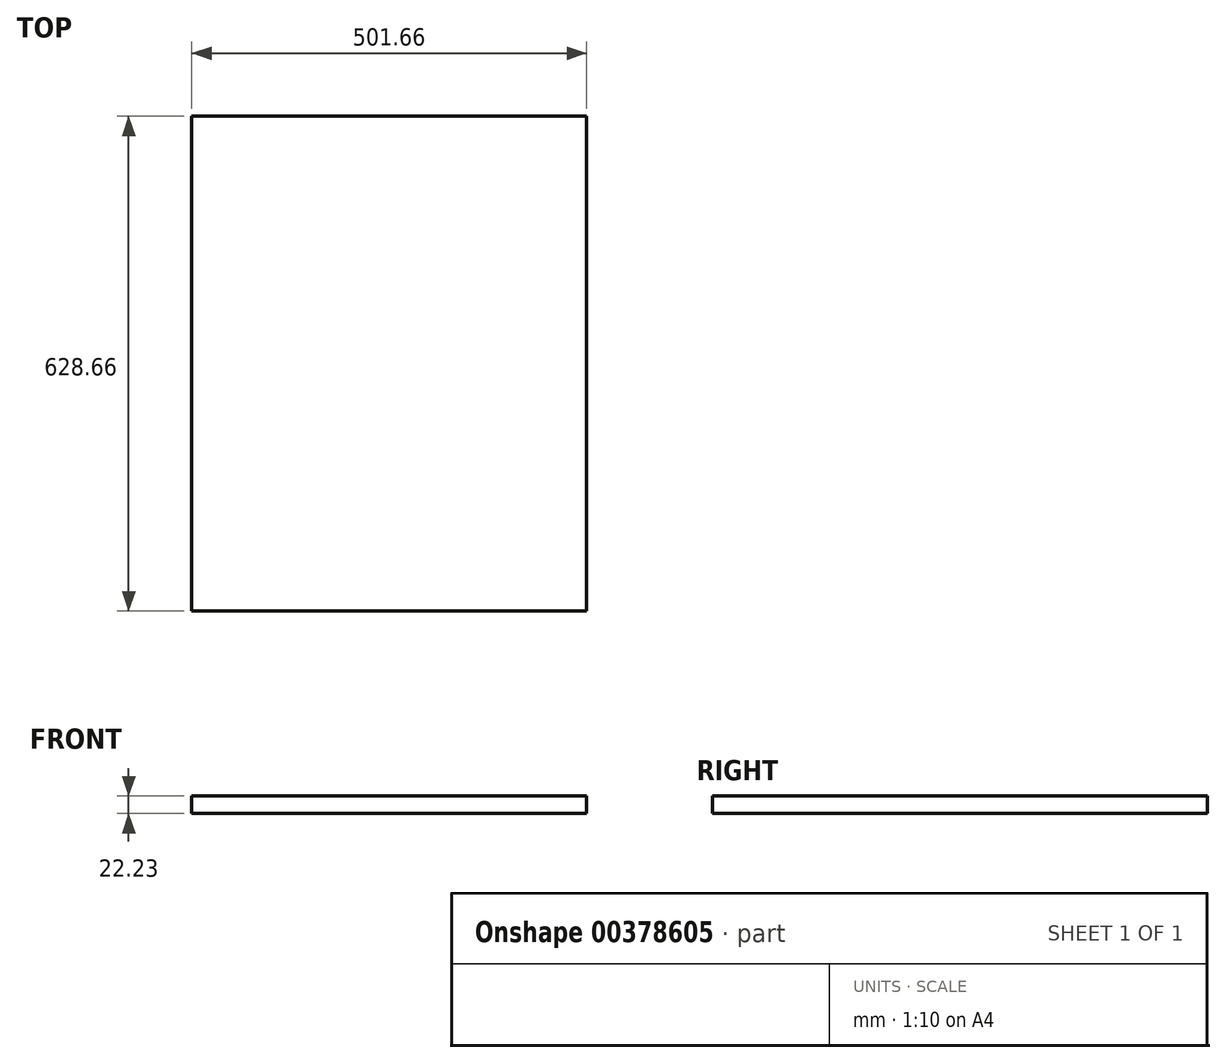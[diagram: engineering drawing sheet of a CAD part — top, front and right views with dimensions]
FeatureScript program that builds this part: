
annotation { "Feature Type Name" : "Feature", "Feature Type Description" : "" }
export const myFeature = defineFeature(function(context is Context, id is Id, definition is map)
    precondition{}
    {
        {
            var Q0;
            Q0=qCreatedBy(makeId("Top.planeOp"),FACE);
            var sketch = newSketch(context, id + "F0", { "sketchPlane" : qUnion([Q0])});
            skLineSegment(sketch, "E0.bottom", {"start": v(250.83, -314.32) * mm, "end": v(-250.82, -314.33) * mm});
            skLineSegment(sketch, "E0.top", {"start": v(250.83, 314.33) * mm, "end": v(-250.82, 314.32) * mm});
            skLineSegment(sketch, "E0.left", {"start": v(250.83, -314.32) * mm, "end": v(250.83, 314.33) * mm});
            skLineSegment(sketch, "E0.right", {"start": v(-250.82, -314.33) * mm, "end": v(-250.82, 314.32) * mm});
            skPoint(sketch, "E0.middle", {"position": v(0, 0) * mm});
            skSolve(sketch);
        }
        {
            var Q0;
            Q0=makeQuery(id+"F0.imprint","IMPRINT",FACE,{"disambiguationData":[TD([[makeQuery(id+"F0.imprint","IMPRINT",EDGE,{"derivedFrom":sQuery(id+"F0.wireOp",EDGE,"E0.bottom")}),-1.0]])]});
            extrude(context, id + "F1", {"entities" : qUnion([Q0]), "depth" : 22.22 * mm, "offsetDistance" : 25.4 * mm});
        }
    });
